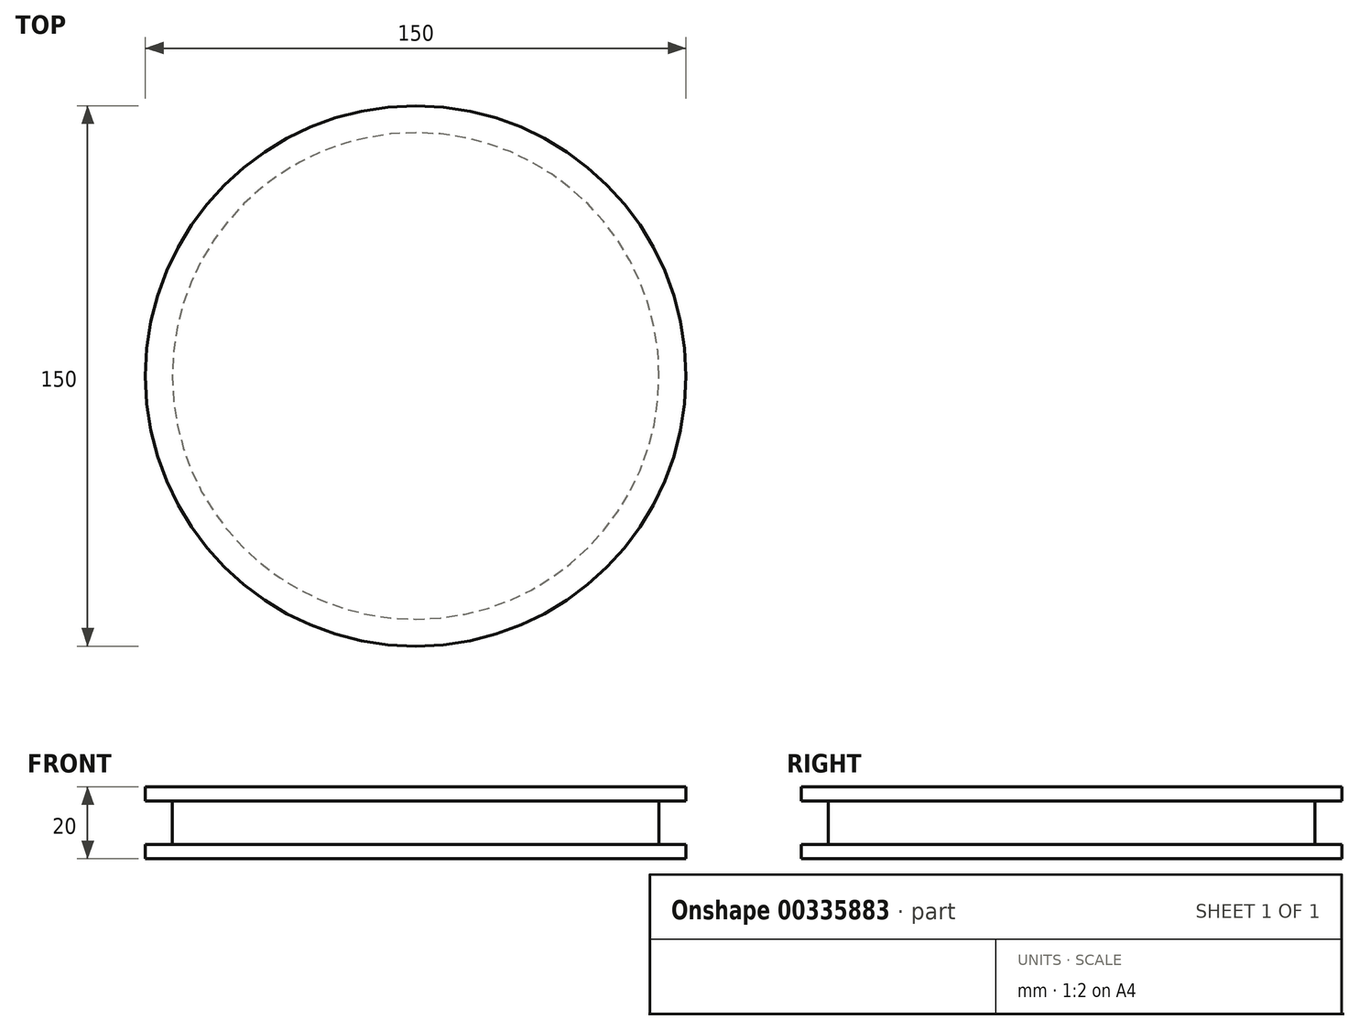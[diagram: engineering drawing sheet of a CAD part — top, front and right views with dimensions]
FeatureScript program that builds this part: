
annotation { "Feature Type Name" : "Feature", "Feature Type Description" : "" }
export const myFeature = defineFeature(function(context is Context, id is Id, definition is map)
    precondition{}
    {
        {
            assignVariable(context, id + "F0", {"name" : "alt_flange", "anyValue" : 4});
        }
        {
            assignVariable(context, id + "F1", {"name" : "alt_cinghia", "anyValue" : 12});
        }
        {
            var Q0;
            Q0=qCreatedBy(makeId("Top.planeOp"),FACE);
            var sketch = newSketch(context, id + "F2", { "sketchPlane" : qUnion([Q0])});
            skCircle(sketch, "E0", {"center": v(0, 0) * mm, "radius": 75 * mm});
            skSolve(sketch);
        }
        {
            var Q0;
            Q0=qSketchRegion(id+"F2",true);
            extrude(context, id + "F3", {"entities" : qUnion([Q0]), "depth" : (getVariable(context, 'alt_flange')) * mm});
        }
        {
            var Q0;
            Q0=qCreatedBy(makeId("Top.planeOp"),FACE);
            cPlane(context, id + "F4", {"entities" : qUnion([Q0]), "cplaneType" : CPlaneType.OFFSET, "offset" : (getVariable(context, 'alt_flange')) * mm, "width" : 150 * mm, "height" : 150 * mm});
        }
        {
            var Q0;
            Q0=qCreatedBy(id+"F4.planeOp",FACE);
            var sketch = newSketch(context, id + "F5", { "sketchPlane" : qUnion([Q0])});
            skCircle(sketch, "E1", {"center": v(0, 0) * mm, "radius": 67.5 * mm});
            skSolve(sketch);
        }
        {
            var Q0;
            Q0=qSketchRegion(id+"F5",true);
            extrude(context, id + "F6", {"entities" : qUnion([Q0]), "operationType" : NewBodyOperationType.ADD, "depth" : (getVariable(context, 'alt_cinghia')) * mm});
        }
        {
            var Q0;
            Q0=qCreatedBy(id+"F4.planeOp",FACE);
            cPlane(context, id + "F7", {"entities" : qUnion([Q0]), "cplaneType" : CPlaneType.OFFSET, "offset" : (getVariable(context, 'alt_cinghia')) * mm, "width" : 150 * mm, "height" : 150 * mm});
        }
        {
            var Q0;
            Q0=qCreatedBy(id+"F7.planeOp",FACE);
            var sketch = newSketch(context, id + "F8", { "sketchPlane" : qUnion([Q0])});
            skCircle(sketch, "E2", {"center": v(0, 0) * mm, "radius": 75 * mm});
            skSolve(sketch);
        }
        {
            var Q0;
            Q0=qSketchRegion(id+"F8",true);
            extrude(context, id + "F9", {"entities" : qUnion([Q0]), "operationType" : NewBodyOperationType.ADD, "depth" : (getVariable(context, 'alt_flange')) * mm});
        }
        {
            var Q0;
            Q0=makeQuery(id+"F3.opExtrude","SWEPT_BODY",BODY,{"disambiguationData":[OSD([sQuery(id+"F2.wireOp",EDGE,"E0")])]});
            transform(context, id + "F10", {"entities" : qUnion([Q0]), "transformType" : TransformType.TRANSLATION_3D, "dx" : 0 * mm, "dy" : 0 * mm, "dz" : (getVariable(context, 'alt_flange') * 2 + getVariable(context, 'alt_cinghia')) * mm, "makeCopy" : true});
        }
        {
            var Q0;
            Q0=makeQuery(id+"F10.opPattern","COPY",BODY,{"derivedFrom":makeQuery(id+"F3.opExtrude","SWEPT_BODY",BODY,{"disambiguationData":[OSD([sQuery(id+"F2.wireOp",EDGE,"E0")])]}),"instanceName":"1"});
            deleteBodies(context, id + "F11", {"entities" : qUnion([Q0])});
        }
        {
            var Q0;
            Q0=makeQuery(id+"F3.opExtrude","SWEPT_BODY",BODY,{"disambiguationData":[OSD([sQuery(id+"F2.wireOp",EDGE,"E0")])]});
            transform(context, id + "F12", {"entities" : qUnion([Q0]), "transformType" : TransformType.COPY});
        }
        {
            var Q0;
            Q0=makeQuery(id+"F12.opPattern","COPY",BODY,{"derivedFrom":makeQuery(id+"F3.opExtrude","SWEPT_BODY",BODY,{"disambiguationData":[OSD([sQuery(id+"F2.wireOp",EDGE,"E0")])]}),"instanceName":"1"});
            deleteBodies(context, id + "F13", {"entities" : qUnion([Q0])});
        }
    });
